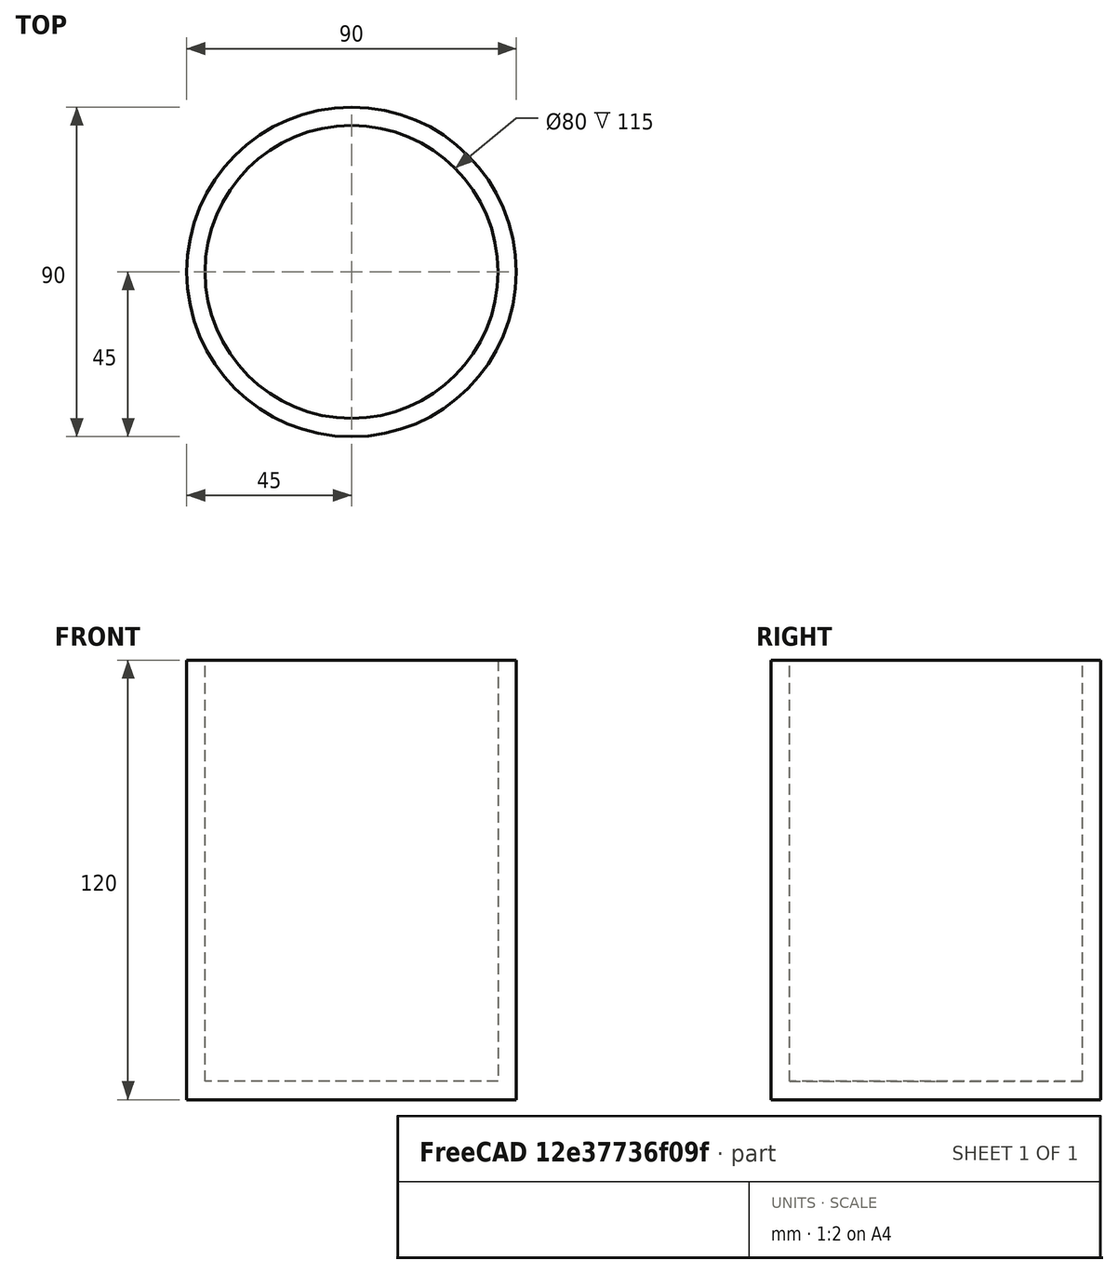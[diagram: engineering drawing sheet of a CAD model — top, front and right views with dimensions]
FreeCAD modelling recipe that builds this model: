
FCSTD DOCUMENT  (FreeCAD 1.0R38641 +678 (Git))
Label: Unnamed
License: All rights reserved
LicenseURL: https://en.wikipedia.org/wiki/All_rights_reserved
objects: Sketcher::SketchObject×2, PartDesign::Pad×1, PartDesign::Pocket×1, PartDesign::Body×1
note: 11 computed .brp shape members not serialized (recipe doc carries the construction recipe); baked Part::Feature solids carry a one-line shape summary decoded from their .brp

FEATURE [Sketcher::SketchObject] Sketch
  ArcFitTolerance = 1e-06
  AttachmentSupport = -> [XY_Plane]
  FullyConstrained = true
  MakeInternals = false
  MapMode = 5
  sketch-geometry (1):
    g0: Circle CenterX=0 CenterY=0 CenterZ=0 NormalX=0 NormalY=0 NormalZ=1 AngleXU=0 Radius=45
  constraints (2):
    c: Diameter(g0) = 90
    c: Coincident(g0,g-1)
FEATURE [PartDesign::Pad] Pad
  Direction = (0,0,1)
  Length = 120
  Length2 = 10
  Profile = -> Sketch
  ReferenceAxis = -> Sketch [N_Axis]
  Refine = true
  Suppressed = false
  Type = 0
FEATURE [Sketcher::SketchObject] Sketch001
  ArcFitTolerance = 1e-06
  AttachmentSupport = -> [Pad]
  FullyConstrained = false
  MakeInternals = false
  MapMode = 5
  Placement = pos=(0,0,120) rot=(0,0,1;0rad)
  sketch-geometry (1):
    g0: Circle CenterX=0 CenterY=0 CenterZ=0 NormalX=0 NormalY=0 NormalZ=1 AngleXU=0 Radius=40
  constraints (1):
    c: Diameter(g0) = 80
FEATURE [PartDesign::Pocket] Pocket
  BaseFeature = -> Pad
  Direction = (0,0,-1)
  Length = 115
  Length2 = 5
  Profile = -> Sketch001
  ReferenceAxis = -> Sketch001 [N_Axis]
  Refine = true
  Suppressed = false
  Type = 0
FEATURE [PartDesign::Body] Body
  AllowCompound = false
  Group = -> [Sketch,Pad,Sketch001,Pocket]
  Origin = -> Origin
  Tip = -> Pocket
